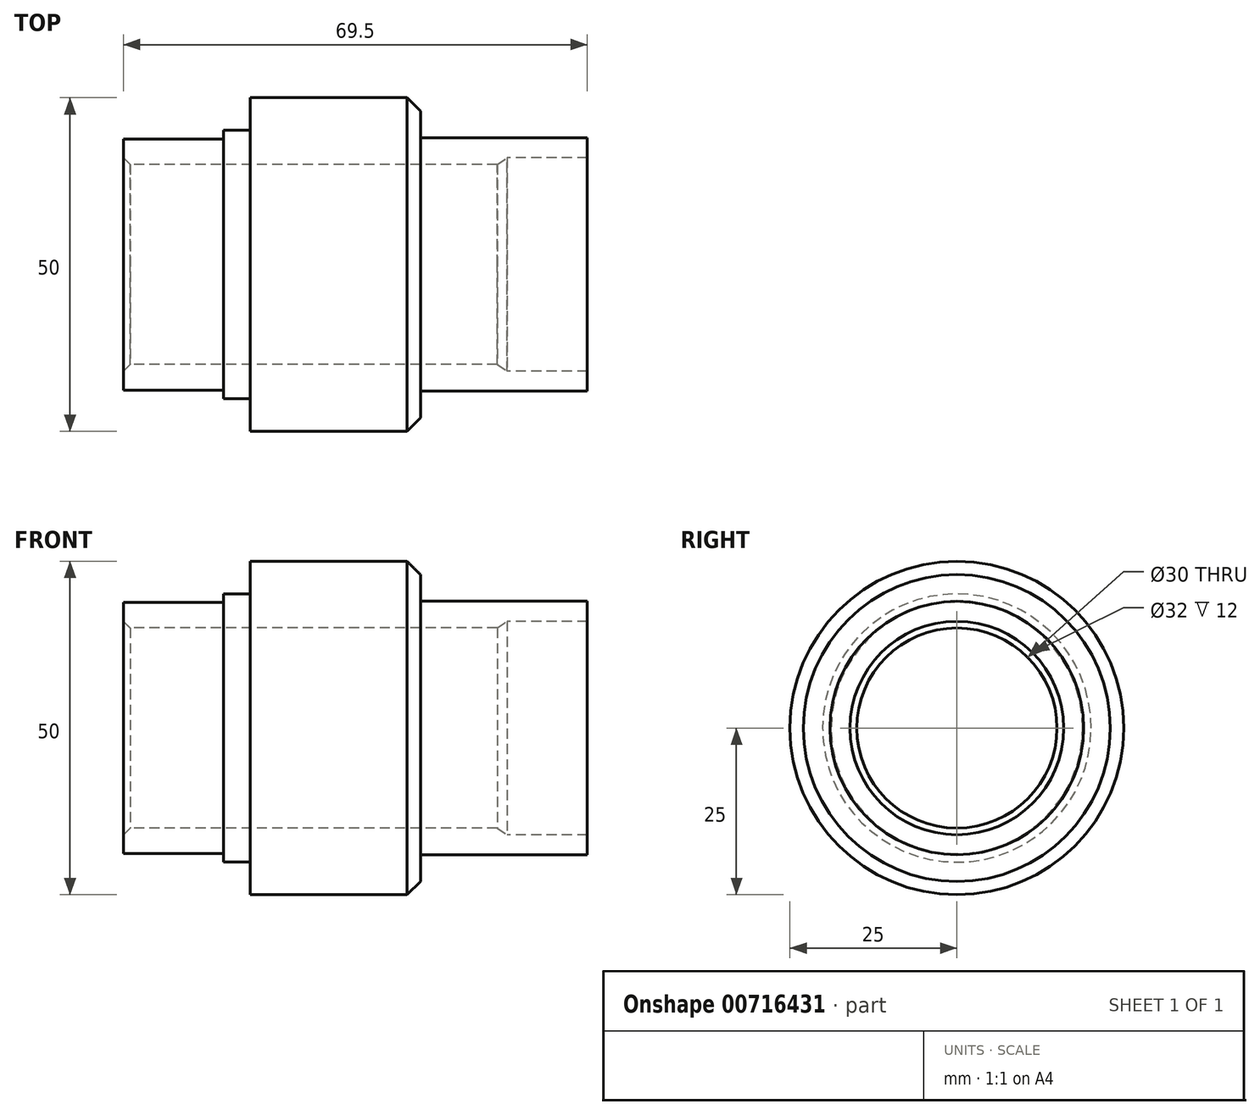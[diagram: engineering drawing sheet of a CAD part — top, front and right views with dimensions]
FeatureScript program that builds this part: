
annotation { "Feature Type Name" : "Feature", "Feature Type Description" : "" }
export const myFeature = defineFeature(function(context is Context, id is Id, definition is map)
    precondition{}
    {
        {
            var Q0;
            Q0=qCreatedBy(makeId("Top.planeOp"),FACE);
            var sketch = newSketch(context, id + "F0", { "sketchPlane" : qUnion([Q0])});
            skLineSegment(sketch, "E0", {"start": v(-54.51, 0) * mm, "end": v(76.36, 0) * mm, "construction": true});
            skLineSegment(sketch, "E1", {"start": v(56, 15) * mm, "end": v(1, 15) * mm});
            skLineSegment(sketch, "E2", {"start": v(0, 16) * mm, "end": v(0, 18.84) * mm});
            skLineSegment(sketch, "E3", {"start": v(0, 18.84) * mm, "end": v(15, 18.84) * mm});
            skLineSegment(sketch, "E4", {"start": v(15, 18.84) * mm, "end": v(15, 20.11) * mm});
            skLineSegment(sketch, "E5", {"start": v(15, 20.11) * mm, "end": v(19, 20.11) * mm});
            skLineSegment(sketch, "E6", {"start": v(19, 20.11) * mm, "end": v(19, 25) * mm});
            skLineSegment(sketch, "E7", {"start": v(19, 25) * mm, "end": v(42.5, 25) * mm});
            skLineSegment(sketch, "E8", {"start": v(44.5, 23) * mm, "end": v(44.5, 19) * mm});
            skLineSegment(sketch, "E9", {"start": v(44.5, 19) * mm, "end": v(69.5, 19) * mm});
            skLineSegment(sketch, "E10", {"start": v(69.5, 19) * mm, "end": v(69.5, 16) * mm});
            skLineSegment(sketch, "E11", {"start": v(69.5, 16) * mm, "end": v(57.5, 16) * mm});
            skLineSegment(sketch, "E12", {"start": v(57.5, 16) * mm, "end": v(56, 15) * mm});
            skLineSegment(sketch, "E13", {"start": v(42.5, 25) * mm, "end": v(44.5, 23) * mm});
            skLineSegment(sketch, "E14", {"start": v(0, 16) * mm, "end": v(1, 15) * mm});
            skSolve(sketch);
        }
        {
            var Q0;
            Q0 = qSketchRegion(id + "F0", true);
            var Q1;
            Q1=sQuery(id+"F0.wireOp",EDGE,"E0");
            revolve(context, id + "F1", {"surfaceOperationType" : NewSurfaceOperationType.NEW, "entities" : qUnion([Q0]), "axis" : qUnion([Q1]), "revolveType" : RevolveType.FULL});
        }
    });
